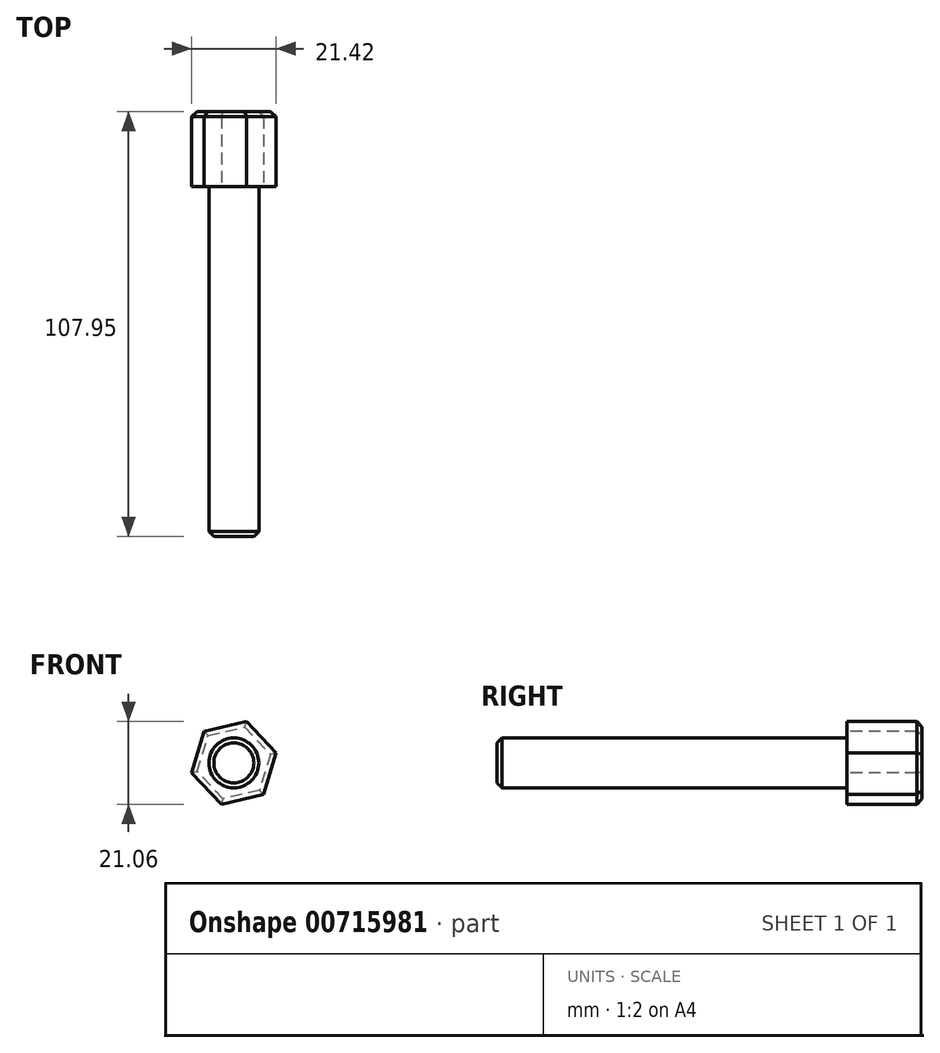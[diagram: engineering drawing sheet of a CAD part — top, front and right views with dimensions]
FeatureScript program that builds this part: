
annotation { "Feature Type Name" : "Feature", "Feature Type Description" : "" }
export const myFeature = defineFeature(function(context is Context, id is Id, definition is map)
    precondition{}
    {
        {
            var Q0;
            Q0=qCreatedBy(makeId("Front.planeOp"),FACE);
            var sketch = newSketch(context, id + "F0", { "sketchPlane" : qUnion([Q0])});
            skCircle(sketch, "E0.cCircle", {"center": v(0, 0) * mm, "radius": 9.53 * mm, "construction": true});
            skLineSegment(sketch, "E0.0", {"start": v(-7.53, 8.02) * mm, "end": v(3.18, 10.53) * mm});
            skLineSegment(sketch, "E0.1", {"start": v(3.18, 10.53) * mm, "end": v(10.7, 2.51) * mm});
            skLineSegment(sketch, "E0.2", {"start": v(10.7, 2.51) * mm, "end": v(7.53, -8.02) * mm});
            skLineSegment(sketch, "E0.3", {"start": v(7.53, -8.02) * mm, "end": v(-3.18, -10.53) * mm});
            skLineSegment(sketch, "E0.4", {"start": v(-3.18, -10.53) * mm, "end": v(-10.7, -2.51) * mm});
            skLineSegment(sketch, "E0.5", {"start": v(-10.7, -2.51) * mm, "end": v(-7.53, 8.02) * mm});
            skPoint(sketch, "E0.0.midPoint", {"position": v(-2.18, 9.27) * mm});
            skSolve(sketch);
        }
        {
            var Q0;
            Q0 = qSketchRegion(id + "F0", true);
            extrude(context, id + "F1", {"entities" : qUnion([Q0]), "oppositeDirection" : true, "depth" : 19.05 * mm, "offsetDistance" : 25.4 * mm});
        }
        {
            var Q0;
            Q0=qCreatedBy(makeId("Front.planeOp"),FACE);
            var sketch = newSketch(context, id + "F2", { "sketchPlane" : qUnion([Q0])});
            skCircle(sketch, "E1", {"center": v(0, 0) * mm, "radius": 6.35 * mm});
            skSolve(sketch);
        }
        {
            var Q0;
            Q0 = qSketchRegion(id + "F2", true);
            extrude(context, id + "F3", {"entities" : qUnion([Q0]), "operationType" : NewBodyOperationType.ADD, "depth" : 88.9 * mm, "offsetDistance" : 25.4 * mm});
        }
        {
            var Q0;
            Q0=makeQuery(id+"F3.opExtrude","CAP_EDGE",EDGE,{"disambiguationData":[OSD([sQuery(id+"F2.wireOp",EDGE,"E1")])],"isStart":false});
            var Q1;
            Q1=makeQuery(id+"F1.opExtrude","CAP_EDGE",EDGE,{"disambiguationData":[OSD([sQuery(id+"F0.wireOp",EDGE,"E0.5")])],"isStart":false});
            var Q2;
            Q2=makeQuery(id+"F1.opExtrude","CAP_FACE",FACE,{"disambiguationData":[OSD([sQuery(id+"F0.wireOp",EDGE,"E0.0"),sQuery(id+"F0.wireOp",EDGE,"E0.1"),sQuery(id+"F0.wireOp",EDGE,"E0.2"),sQuery(id+"F0.wireOp",EDGE,"E0.3"),sQuery(id+"F0.wireOp",EDGE,"E0.4"),sQuery(id+"F0.wireOp",EDGE,"E0.5")])],"isStart":false});
            chamfer(context, id + "F4", {"entities" : qUnion([Q0, Q1, Q2]), "width" : 1.27 * mm, "tangentPropagation" : true});
        }
    });
